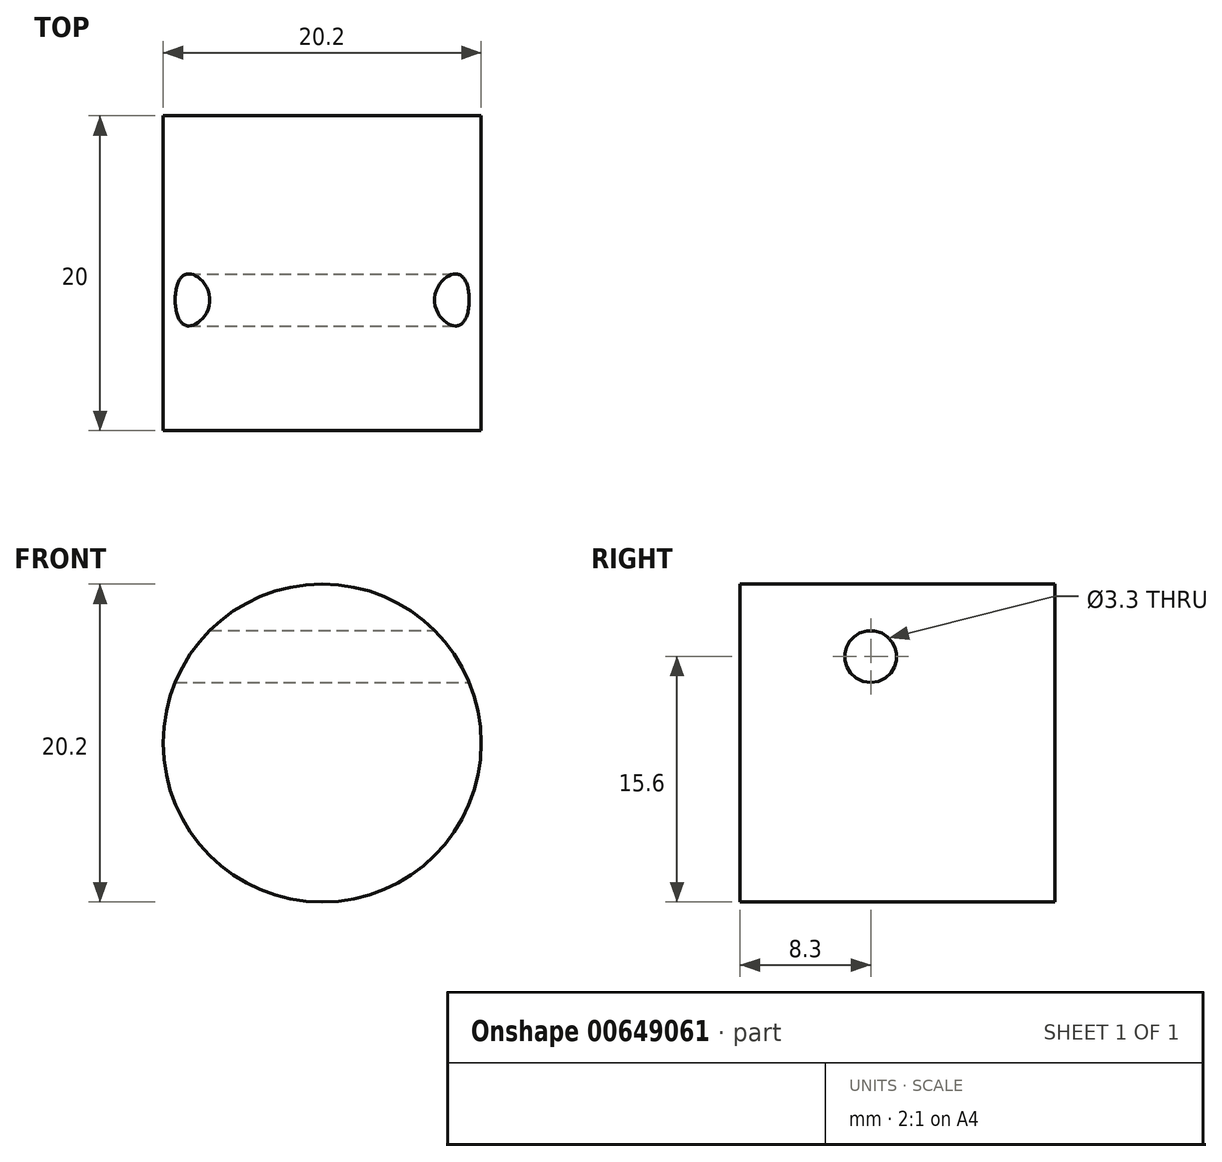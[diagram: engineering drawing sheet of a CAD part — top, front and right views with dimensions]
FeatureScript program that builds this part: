
annotation { "Feature Type Name" : "Feature", "Feature Type Description" : "" }
export const myFeature = defineFeature(function(context is Context, id is Id, definition is map)
    precondition{}
    {
        {
            var Q0;
            Q0=qCreatedBy(makeId("Front.planeOp"),FACE);
            var sketch = newSketch(context, id + "F0", { "sketchPlane" : qUnion([Q0])});
            skCircle(sketch, "E0", {"center": v(0, 0) * mm, "radius": 10.1 * mm});
            skSolve(sketch);
        }
        {
            var Q0;
            Q0 = qSketchRegion(id + "F0", true);
            extrude(context, id + "F1", {"entities" : qUnion([Q0]), "depth" : 20 * mm, "offsetDistance" : 25 * mm});
        }
        {
            var Q0;
            Q0=qCreatedBy(makeId("Right.planeOp"),FACE);
            var sketch = newSketch(context, id + "F2", { "sketchPlane" : qUnion([Q0])});
            skCircle(sketch, "E1", {"center": v(-11.7, 5.5) * mm, "radius": 1.65 * mm});
            skLineSegment(sketch, "E2.0", {"start": v(-20, -10.1) * mm, "end": v(-20, 10.1) * mm});
            skPoint(sketch, "E3", {"position": v(-20, 0) * mm});
            skLineSegment(sketch, "E4", {"start": v(-20, 0) * mm, "end": v(-9.75, 0) * mm, "construction": true});
            skSolve(sketch);
        }
        {
            var Q0;
            Q0 = qSketchRegion(id + "F2", true);
            extrude(context, id + "F3", {"entities" : qUnion([Q0]), "operationType" : NewBodyOperationType.REMOVE, "endBound" : BoundingType.SYMMETRIC, "oppositeDirection" : true, "depth" : 22.9 * mm, "offsetDistance" : 25 * mm});
        }
    });
